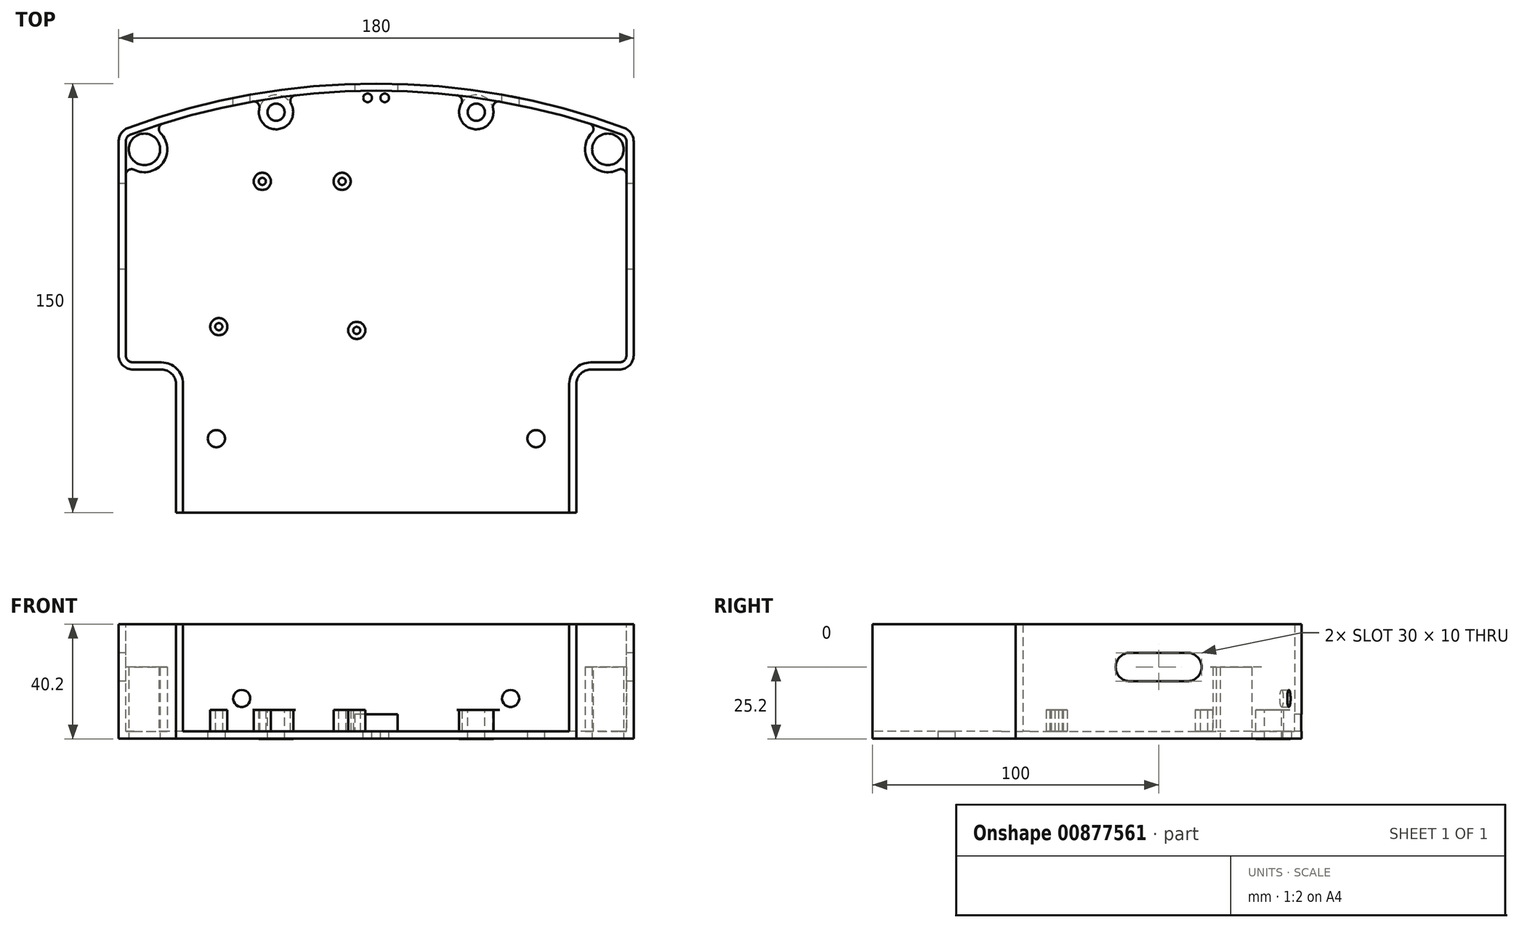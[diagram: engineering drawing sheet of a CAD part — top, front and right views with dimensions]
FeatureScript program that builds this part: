
annotation { "Feature Type Name" : "Feature", "Feature Type Description" : "" }
export const myFeature = defineFeature(function(context is Context, id is Id, definition is map)
    precondition{}
    {
        {
            var Q0;
            Q0=qCreatedBy(makeId("Top.planeOp"),FACE);
            var sketch = newSketch(context, id + "F0", { "sketchPlane" : qUnion([Q0])});
            skLineSegment(sketch, "E0.bottom", {"start": v(-90, -50) * mm, "end": v(90, -50) * mm});
            skLineSegment(sketch, "E0.top", {"start": v(-90, 100) * mm, "end": v(90, 100) * mm});
            skLineSegment(sketch, "E0.left", {"start": v(-90, -50) * mm, "end": v(-90, 100) * mm});
            skLineSegment(sketch, "E0.right", {"start": v(90, -50) * mm, "end": v(90, 100) * mm});
            skCircle(sketch, "E1", {"center": v(0, -150) * mm, "radius": 250 * mm});
            skSolve(sketch);
        }
        {
            var Q0;
            {var subQ4=sQuery(id+"F0.wireOp",EDGE,"E0.bottom");Q0=makeQuery(id+"F0.imprint","IMPRINT",FACE,{"disambiguationData":[TD([[makeQuery(id+"F0.imprint","IMPRINT",EDGE,{"derivedFrom":subQ4}),1.0]])]});}
            extrude(context, id + "F1", {"entities" : qUnion([Q0]), "depth" : 40 * mm});
        }
        {
            var Q0;
            Q0=qCreatedBy(makeId("Top.planeOp"),FACE);
            var sketch = newSketch(context, id + "F2", { "sketchPlane" : qUnion([Q0])});
            skLineSegment(sketch, "E2.bottom", {"start": v(-170, 0) * mm, "end": v(-70, 0) * mm});
            skLineSegment(sketch, "E2.top", {"start": v(-170, -200) * mm, "end": v(-70, -200) * mm});
            skLineSegment(sketch, "E2.left", {"start": v(-170, 0) * mm, "end": v(-170, -200) * mm});
            skLineSegment(sketch, "E2.right", {"start": v(-70, 0) * mm, "end": v(-70, -200) * mm});
            skLineSegment(sketch, "E3.bottom", {"start": v(170, 0) * mm, "end": v(70, 0) * mm});
            skLineSegment(sketch, "E3.top", {"start": v(170, -200) * mm, "end": v(70, -200) * mm});
            skLineSegment(sketch, "E3.left", {"start": v(170, 0) * mm, "end": v(170, -200) * mm});
            skLineSegment(sketch, "E3.right", {"start": v(70, 0) * mm, "end": v(70, -200) * mm});
            skSolve(sketch);
        }
        {
            var Q0;
            Q0=makeQuery(id+"F2.imprint","IMPRINT",FACE,{"disambiguationData":[TD([[makeQuery(id+"F2.imprint","IMPRINT",EDGE,{"derivedFrom":sQuery(id+"F2.wireOp",EDGE,"E2.bottom")}),-1.0]])]});
            var Q1;
            Q1=makeQuery(id+"F2.imprint","IMPRINT",FACE,{"disambiguationData":[TD([[makeQuery(id+"F2.imprint","IMPRINT",EDGE,{"derivedFrom":sQuery(id+"F2.wireOp",EDGE,"E3.bottom")}),1.0]])]});
            extrude(context, id + "F3", {"entities" : qUnion([Q0, Q1]), "operationType" : NewBodyOperationType.REMOVE, "depth" : 100 * mm});
        }
        {
            var Q0;
            Q0=makeQuery(id+"F1.opExtrude","SWEPT_EDGE",EDGE,{"disambiguationData":[OSD([sQuery(id+"F0.wireOp",EDGE,"E0.left"),sQuery(id+"F0.wireOp",EDGE,"E1")])]});
            var Q1;
            Q1=makeQuery(id+"F1.opExtrude","SWEPT_EDGE",EDGE,{"disambiguationData":[OSD([sQuery(id+"F0.wireOp",EDGE,"E0.right"),sQuery(id+"F0.wireOp",EDGE,"E1")])]});
            var Q2;
            Q2=makeQuery(id+"F3.boolean.opBoolean","INTERSECT",EDGE,{"derivedFrom":[makeQuery(id+"F1.opExtrude","SWEPT_FACE",FACE,{"disambiguationData":[OSD([sQuery(id+"F0.wireOp",EDGE,"E0.right")])]}),makeQuery(id+"F3.opExtrude","SWEPT_FACE",FACE,{"disambiguationData":[OSD([sQuery(id+"F2.wireOp",EDGE,"E3.bottom")])]})]});
            var Q3;
            Q3=makeQuery(id+"F3.boolean.opBoolean","COPY",EDGE,{"derivedFrom":makeQuery(id+"F3.opExtrude","SWEPT_EDGE",EDGE,{"disambiguationData":[OSD([sQuery(id+"F2.wireOp",EDGE,"E3.bottom"),sQuery(id+"F2.wireOp",EDGE,"E3.right")])]})});
            var Q4;
            Q4=makeQuery(id+"F3.boolean.opBoolean","INTERSECT",EDGE,{"derivedFrom":[makeQuery(id+"F1.opExtrude","SWEPT_FACE",FACE,{"disambiguationData":[OSD([sQuery(id+"F0.wireOp",EDGE,"E0.left")])]}),makeQuery(id+"F3.opExtrude","SWEPT_FACE",FACE,{"disambiguationData":[OSD([sQuery(id+"F2.wireOp",EDGE,"E2.bottom")])]})]});
            var Q5;
            Q5=makeQuery(id+"F3.boolean.opBoolean","COPY",EDGE,{"derivedFrom":makeQuery(id+"F3.opExtrude","SWEPT_EDGE",EDGE,{"disambiguationData":[OSD([sQuery(id+"F2.wireOp",EDGE,"E2.bottom"),sQuery(id+"F2.wireOp",EDGE,"E2.right")])]})});
            fillet(context, id + "F4", {"entities" : qUnion([Q0, Q1, Q2, Q3, Q4, Q5]), "radius" : 5 * mm, "tangentPropagation" : true, "allowEdgeOverflow" : false});
        }
        {
            var Q0;
            Q0=makeQuery(id+"F1.opExtrude","CAP_FACE",FACE,{"disambiguationData":[OSD([sQuery(id+"F0.wireOp",EDGE,"E0.bottom"),sQuery(id+"F0.wireOp",EDGE,"E0.left"),sQuery(id+"F0.wireOp",EDGE,"E0.right"),sQuery(id+"F0.wireOp",EDGE,"E1")])],"isStart":false});
            var Q1;
            Q1=makeQuery(id+"F1.opExtrude","SWEPT_FACE",FACE,{"disambiguationData":[OSD([sQuery(id+"F0.wireOp",EDGE,"E0.bottom")])]});
            shell(context, id + "F5", {"entities" : qUnion([Q0, Q1]), "thickness" : 2.5 * mm});
        }
        {
            var Q0;
            Q0=qCreatedBy(makeId("Top.planeOp"),FACE);
            var sketch = newSketch(context, id + "F6", { "sketchPlane" : qUnion([Q0])});
            skCircle(sketch, "E4", {"center": v(-55.86, -24.14) * mm, "radius": 3 * mm});
            skCircle(sketch, "E5", {"center": v(55.86, -24.14) * mm, "radius": 3 * mm});
            skLineSegment(sketch, "E6", {"start": v(0, -80) * mm, "end": v(-55.86, -24.14) * mm, "construction": true});
            skLineSegment(sketch, "E7", {"start": v(0, -80) * mm, "end": v(55.86, -24.14) * mm, "construction": true});
            skSolve(sketch);
        }
        {
            var Q0;
            Q0=qSketchRegion(id+"F6",true);
            extrude(context, id + "F7", {"entities" : qUnion([Q0]), "operationType" : NewBodyOperationType.REMOVE, "depth" : 25 * mm});
        }
        {
            var Q0;
            Q0=qCreatedBy(makeId("Top.planeOp"),FACE);
            var sketch = newSketch(context, id + "F8", { "sketchPlane" : qUnion([Q0])});
            skCircle(sketch, "E8", {"center": v(-81, 77) * mm, "radius": 8 * mm});
            skCircle(sketch, "E9", {"center": v(81, 77) * mm, "radius": 8 * mm});
            skSolve(sketch);
        }
        {
            var Q0;
            Q0=qSketchRegion(id+"F8",true);
            extrude(context, id + "F9", {"entities" : qUnion([Q0]), "operationType" : NewBodyOperationType.ADD, "depth" : 25 * mm});
        }
        {
            var Q0;
            Q0=qCreatedBy(makeId("Top.planeOp"),FACE);
            var sketch = newSketch(context, id + "F10", { "sketchPlane" : qUnion([Q0])});
            skCircle(sketch, "E10", {"center": v(-81, 77) * mm, "radius": 5.5 * mm});
            skCircle(sketch, "E11", {"center": v(81, 77) * mm, "radius": 5.5 * mm});
            skSolve(sketch);
        }
        {
            var Q0;
            Q0=qSketchRegion(id+"F10",true);
            extrude(context, id + "F11", {"entities" : qUnion([Q0]), "operationType" : NewBodyOperationType.REMOVE, "depth" : 25 * mm});
        }
        {
            var Q0;
            Q0=qCreatedBy(makeId("Top.planeOp"),FACE);
            var sketch = newSketch(context, id + "F12", { "sketchPlane" : qUnion([Q0])});
            skCircle(sketch, "E12", {"center": v(-55, 15) * mm, "radius": 3 * mm});
            skCircle(sketch, "E13", {"center": v(-55, 15) * mm, "radius": 1.25 * mm});
            skCircle(sketch, "E14", {"center": v(-39.8, 65.8) * mm, "radius": 1.25 * mm});
            skCircle(sketch, "E15", {"center": v(-39.8, 65.8) * mm, "radius": 3 * mm});
            skCircle(sketch, "E16", {"center": v(-11.9, 65.8) * mm, "radius": 1.25 * mm});
            skCircle(sketch, "E17", {"center": v(-11.9, 65.8) * mm, "radius": 3 * mm});
            skCircle(sketch, "E18", {"center": v(-6.8, 13.7) * mm, "radius": 1.25 * mm});
            skCircle(sketch, "E19", {"center": v(-6.8, 13.7) * mm, "radius": 3 * mm});
            skSolve(sketch);
        }
        {
            var Q0;
            Q0=qSketchRegion(id+"F12",true);
            extrude(context, id + "F13", {"entities" : qUnion([Q0]), "operationType" : NewBodyOperationType.ADD, "depth" : 10 * mm});
        }
        {
            var Q0;
            Q0=qCreatedBy(makeId("Front.planeOp"),FACE);
            var sketch = newSketch(context, id + "F14", { "sketchPlane" : qUnion([Q0])});
            skCircle(sketch, "E20", {"center": v(47, 14) * mm, "radius": 3 * mm});
            skCircle(sketch, "E21", {"center": v(-47, 14) * mm, "radius": 3 * mm});
            skSolve(sketch);
        }
        {
            var Q0;
            Q0=qSketchRegion(id+"F14",true);
            extrude(context, id + "F15", {"entities" : qUnion([Q0]), "operationType" : NewBodyOperationType.REMOVE, "endBound" : BoundingType.SYMMETRIC, "depth" : 300 * mm});
        }
        {
            var Q0;
            Q0=qCreatedBy(makeId("Front.planeOp"),FACE);
            var sketch = newSketch(context, id + "F16", { "sketchPlane" : qUnion([Q0])});
            skLineSegment(sketch, "E22.bottom", {"start": v(7.5, 8.5) * mm, "end": v(-7.5, 8.5) * mm});
            skLineSegment(sketch, "E22.top", {"start": v(7.5, 2.5) * mm, "end": v(-7.5, 2.5) * mm});
            skLineSegment(sketch, "E22.left", {"start": v(7.5, 8.5) * mm, "end": v(7.5, 2.5) * mm});
            skLineSegment(sketch, "E22.right", {"start": v(-7.5, 8.5) * mm, "end": v(-7.5, 2.5) * mm});
            skSolve(sketch);
        }
        {
            var Q0;
            Q0=makeQuery(id+"F16.imprint","IMPRINT",FACE,{"disambiguationData":[TD([[makeQuery(id+"F16.imprint","IMPRINT",EDGE,{"derivedFrom":sQuery(id+"F16.wireOp",EDGE,"E22.bottom")}),1.0]])]});
            extrude(context, id + "F17", {"entities" : qUnion([Q0]), "operationType" : NewBodyOperationType.REMOVE, "oppositeDirection" : true, "depth" : 250 * mm, "hasSecondDirection" : true, "secondDirectionOppositeDirection" : true, "secondDirectionDepth" : 41.95 * mm});
        }
        {
            var Q0;
            Q0=qCreatedBy(makeId("Top.planeOp"),FACE);
            var sketch = newSketch(context, id + "F18", { "sketchPlane" : qUnion([Q0])});
            skCircle(sketch, "E23", {"center": v(3, 95) * mm, "radius": 1.5 * mm});
            skCircle(sketch, "E24", {"center": v(-3, 95) * mm, "radius": 1.5 * mm});
            skSolve(sketch);
        }
        {
            var Q0;
            Q0=makeQuery(id+"F18.imprint","IMPRINT",FACE,{"disambiguationData":[TD([[makeQuery(id+"F18.imprint","IMPRINT",EDGE,{"derivedFrom":sQuery(id+"F18.wireOp",EDGE,"E24")}),1.0]])]});
            var Q1;
            Q1=makeQuery(id+"F18.imprint","IMPRINT",FACE,{"disambiguationData":[TD([[makeQuery(id+"F18.imprint","IMPRINT",EDGE,{"derivedFrom":sQuery(id+"F18.wireOp",EDGE,"E23")}),1.0]])]});
            extrude(context, id + "F19", {"entities" : qUnion([Q0, Q1]), "operationType" : NewBodyOperationType.REMOVE, "endBound" : BoundingType.SYMMETRIC, "oppositeDirection" : true, "depth" : 25 * mm});
        }
        {
            var Q0;
            Q0=qCreatedBy(makeId("Top.planeOp"),FACE);
            var sketch = newSketch(context, id + "F20", { "sketchPlane" : qUnion([Q0])});
            skCircle(sketch, "E25", {"center": v(-35, 90) * mm, "radius": 6 * mm});
            skCircle(sketch, "E26", {"center": v(35, 90) * mm, "radius": 6 * mm});
            skSolve(sketch);
        }
        {
            var Q0;
            Q0=qSketchRegion(id+"F20",true);
            extrude(context, id + "F21", {"entities" : qUnion([Q0]), "operationType" : NewBodyOperationType.ADD, "oppositeDirection" : true, "depth" : .2 * mm, "hasSecondDirection" : true, "secondDirectionOppositeDirection" : false, "secondDirectionDepth" : 10 * mm});
        }
        {
            var Q0;
            Q0=makeQuery(id+"F1.opExtrude","CAP_FACE",FACE,{"disambiguationData":[OSD([sQuery(id+"F0.wireOp",EDGE,"E0.bottom"),sQuery(id+"F0.wireOp",EDGE,"E0.left"),sQuery(id+"F0.wireOp",EDGE,"E0.right"),sQuery(id+"F0.wireOp",EDGE,"E1")])],"isStart":true});
            var sketch = newSketch(context, id + "F22", { "sketchPlane" : qUnion([Q0])});
            skCircle(sketch, "E27", {"center": v(-35, -90) * mm, "radius": 3 * mm});
            skCircle(sketch, "E28", {"center": v(35, -90) * mm, "radius": 3 * mm});
            skSolve(sketch);
        }
        {
            var Q0;
            Q0=qSketchRegion(id+"F22",true);
            extrude(context, id + "F23", {"entities" : qUnion([Q0]), "operationType" : NewBodyOperationType.REMOVE, "endBound" : BoundingType.SYMMETRIC, "depth" : 25 * mm});
        }
        {
            var Q0;
            Q0=makeQuery(id+"F9.boolean.opBoolean","INTERSECT",EDGE,{"derivedFrom":[makeQuery(id+"F5.opShell","OFFSET_FACE",FACE,{"disambiguationData":[OSD([sQuery(id+"F0.wireOp",EDGE,"E0.left")])]}),makeQuery(id+"F9.opExtrude","SWEPT_FACE",FACE,{"disambiguationData":[OSD([sQuery(id+"F8.wireOp",EDGE,"E8")])]})]});
            var Q1;
            Q1=makeQuery(id+"F9.boolean.opBoolean","INTERSECT",EDGE,{"derivedFrom":[makeQuery(id+"F5.opShell","OFFSET_FACE",FACE,{"disambiguationData":[OSD([sQuery(id+"F0.wireOp",EDGE,"E1")])]}),makeQuery(id+"F9.opExtrude","SWEPT_FACE",FACE,{"disambiguationData":[OSD([sQuery(id+"F8.wireOp",EDGE,"E8")])]})]});
            var Q2;
            Q2=makeQuery(id+"F21.boolean.opBoolean","INTERSECT",EDGE,{"disambiguationData":[OD(0.0)],"derivedFrom":[makeQuery(id+"F5.opShell","OFFSET_FACE",FACE,{"disambiguationData":[OSD([sQuery(id+"F0.wireOp",EDGE,"E1")])]}),makeQuery(id+"F21.opExtrude","SWEPT_FACE",FACE,{"disambiguationData":[OSD([sQuery(id+"F20.wireOp",EDGE,"E25")])]})]});
            var Q3;
            Q3=makeQuery(id+"F21.boolean.opBoolean","INTERSECT",EDGE,{"disambiguationData":[OD(1.0)],"derivedFrom":[makeQuery(id+"F5.opShell","OFFSET_FACE",FACE,{"disambiguationData":[OSD([sQuery(id+"F0.wireOp",EDGE,"E1")])]}),makeQuery(id+"F21.opExtrude","SWEPT_FACE",FACE,{"disambiguationData":[OSD([sQuery(id+"F20.wireOp",EDGE,"E25")])]})]});
            var Q4;
            Q4=makeQuery(id+"F21.boolean.opBoolean","INTERSECT",EDGE,{"disambiguationData":[OD(1.0)],"derivedFrom":[makeQuery(id+"F5.opShell","OFFSET_FACE",FACE,{"disambiguationData":[OSD([sQuery(id+"F0.wireOp",EDGE,"E1")])]}),makeQuery(id+"F21.opExtrude","SWEPT_FACE",FACE,{"disambiguationData":[OSD([sQuery(id+"F20.wireOp",EDGE,"E26")])]})]});
            var Q5;
            Q5=makeQuery(id+"F21.boolean.opBoolean","INTERSECT",EDGE,{"disambiguationData":[OD(0.0)],"derivedFrom":[makeQuery(id+"F5.opShell","OFFSET_FACE",FACE,{"disambiguationData":[OSD([sQuery(id+"F0.wireOp",EDGE,"E1")])]}),makeQuery(id+"F21.opExtrude","SWEPT_FACE",FACE,{"disambiguationData":[OSD([sQuery(id+"F20.wireOp",EDGE,"E26")])]})]});
            var Q6;
            Q6=makeQuery(id+"F9.boolean.opBoolean","INTERSECT",EDGE,{"derivedFrom":[makeQuery(id+"F5.opShell","OFFSET_FACE",FACE,{"disambiguationData":[OSD([sQuery(id+"F0.wireOp",EDGE,"E1")])]}),makeQuery(id+"F9.opExtrude","SWEPT_FACE",FACE,{"disambiguationData":[OSD([sQuery(id+"F8.wireOp",EDGE,"E9")])]})]});
            var Q7;
            Q7=makeQuery(id+"F9.boolean.opBoolean","INTERSECT",EDGE,{"derivedFrom":[makeQuery(id+"F5.opShell","OFFSET_FACE",FACE,{"disambiguationData":[OSD([sQuery(id+"F0.wireOp",EDGE,"E0.right")])]}),makeQuery(id+"F9.opExtrude","SWEPT_FACE",FACE,{"disambiguationData":[OSD([sQuery(id+"F8.wireOp",EDGE,"E9")])]})]});
            fillet(context, id + "F24", {"entities" : qUnion([Q0, Q1, Q2, Q3, Q4, Q5, Q6, Q7]), "radius" : 2 * mm, "tangentPropagation" : true, "allowEdgeOverflow" : false});
        }
        {
            var Q0;
            Q0=qCreatedBy(makeId("Right.planeOp"),FACE);
            var sketch = newSketch(context, id + "F25", { "sketchPlane" : qUnion([Q0])});
            skLineSegment(sketch, "E29.bottom", {"start": v(40, 30) * mm, "end": v(60, 30) * mm});
            skLineSegment(sketch, "E29.top", {"start": v(40, 20) * mm, "end": v(60, 20) * mm});
            skLineSegment(sketch, "E29.left", {"start": v(40, 30) * mm, "end": v(40, 20) * mm});
            skLineSegment(sketch, "E29.right", {"start": v(60, 30) * mm, "end": v(60, 20) * mm});
            skCircle(sketch, "E30", {"center": v(40, 25) * mm, "radius": 5 * mm});
            skCircle(sketch, "E31", {"center": v(60, 25) * mm, "radius": 5 * mm});
            skSolve(sketch);
        }
        {
            var Q0;
            {var subQ0=sQuery(id+"F25.wireOp",EDGE,"E29.left");Q0=makeQuery(id+"F25.imprint","IMPRINT",FACE,{"disambiguationData":[TD([[makeQuery(id+"F25.imprint","IMPRINT",EDGE,{"derivedFrom":subQ0}),-1.0]])]});}
            var Q1;
            {var subQ0=sQuery(id+"F25.wireOp",EDGE,"E29.right");Q1=makeQuery(id+"F25.imprint","IMPRINT",FACE,{"disambiguationData":[TD([[makeQuery(id+"F25.imprint","IMPRINT",EDGE,{"derivedFrom":subQ0}),1.0]])]});}
            var Q2;
            {var subQ0=sQuery(id+"F25.wireOp",EDGE,"E29.bottom");Q2=makeQuery(id+"F25.imprint","IMPRINT",FACE,{"disambiguationData":[TD([[makeQuery(id+"F25.imprint","IMPRINT",EDGE,{"derivedFrom":subQ0}),-1.0]])]});}
            var Q3;
            {var subQ0=sQuery(id+"F25.wireOp",EDGE,"E29.left");Q3=makeQuery(id+"F25.imprint","IMPRINT",FACE,{"disambiguationData":[TD([[makeQuery(id+"F25.imprint","IMPRINT",EDGE,{"derivedFrom":subQ0}),1.0]])]});}
            var Q4;
            {var subQ0=sQuery(id+"F25.wireOp",EDGE,"E29.right");Q4=makeQuery(id+"F25.imprint","IMPRINT",FACE,{"disambiguationData":[TD([[makeQuery(id+"F25.imprint","IMPRINT",EDGE,{"derivedFrom":subQ0}),-1.0]])]});}
            extrude(context, id + "F26", {"entities" : qUnion([Q0, Q1, Q2, Q3, Q4]), "operationType" : NewBodyOperationType.REMOVE, "endBound" : BoundingType.SYMMETRIC, "depth" : 300 * mm});
        }
    });
